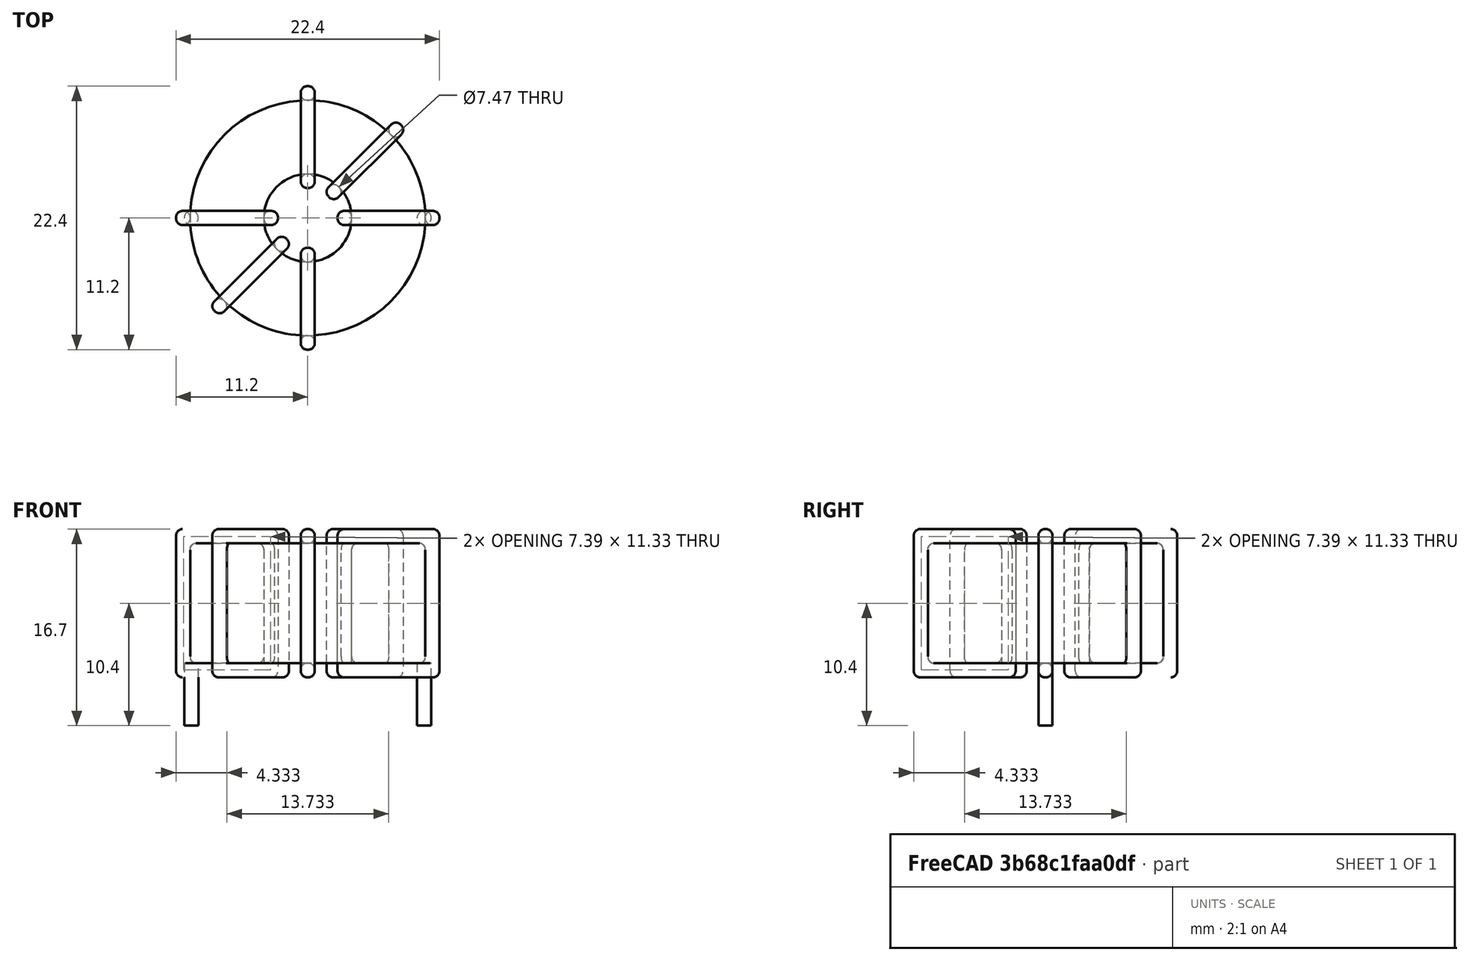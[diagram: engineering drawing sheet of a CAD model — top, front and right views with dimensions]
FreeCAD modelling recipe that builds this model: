
FCSTD DOCUMENT  (FreeCAD 0.16R6703 (Git))
Label: L_Toroid_Horizontal_D22.4mm_P19.80mm_Vishay_TJ4
License: All rights reserved
LicenseURL: http://en.wikipedia.org/wiki/All_rights_reserved
objects: Sketcher::SketchObject×6, PartDesign::Pad×6, PartDesign::Fillet×5, Spreadsheet::Sheet×1
note: 23 computed .brp shape members not serialized (recipe doc carries the construction recipe); baked Part::Feature solids carry a one-line shape summary decoded from their .brp

FEATURE [Spreadsheet::Sheet] Spreadsheet  label="dimensions"
  cells = A1=Wx; B1(Wx)=22.4; C1(WW)=7.466666666666666; D1=22.4; A2=Wy; B2(Wy)=22.4; D2=22.4; A3=RM; B3(RMx)=19.8; C3(RMy)=0; A4=d_wire; B4(d_wire)=1.2; A5=H; B5(H)=10.2; A6=offsetx; B6(offsetx)=1.299999999999999
FEATURE [Sketcher::SketchObject] Sketch
  Placement = pos=(0,0,1.7) rot=(0,0,1;0rad)
  expr: Placement.Base.z = 0.5 + Spreadsheet.d_wire
  expr: Constraints[0] = Spreadsheet.Wx / 2 - Spreadsheet.d_wire
  expr: Constraints[4] = Spreadsheet.WW / 2
  expr: Constraints[2] = Spreadsheet.RMy / 2
  expr: Constraints[1] = Spreadsheet.RMx / 2
  sketch-geometry (2):
    g0: Circle CenterX=9.9 CenterY=0 CenterZ=0 NormalX=0 NormalY=0 NormalZ=1 Radius=10
    g1: Circle CenterX=9.9 CenterY=0 CenterZ=0 NormalX=0 NormalY=0 NormalZ=1 Radius=3.73333
  constraints (5):
    c: Radius(g0) = 10
    c: DistanceX(g-1,g0) = 9.9
    c: DistanceY(g-1,g0) = 0
    c: Coincident(g1,g0)
    c: Radius(g1) = 3.73333
FEATURE [PartDesign::Pad] Pad
  Length = 10.2
  Length2 = 100
  Placement = pos=(0,0,1.7) rot=(0,0,1;0rad)
  Sketch = -> Sketch
  Type = 0
  expr: Length = Spreadsheet.H
FEATURE [Sketcher::SketchObject] Sketch001
  Placement = pos=(0,0,1.1) rot=(0,0,1;0rad)
  expr: Placement.Base.z = 0.5 + Spreadsheet.d_wire * 0.5
  expr: Constraints[4] = Spreadsheet.RMx
  expr: Constraints[2] = Spreadsheet.RMy
  expr: Constraints[1] = Spreadsheet.d_wire / 2
  sketch-geometry (2):
    g0: Circle CenterX=0 CenterY=0 CenterZ=0 NormalX=0 NormalY=0 NormalZ=1 Radius=0.6
    g1: Circle CenterX=19.8 CenterY=0 CenterZ=0 NormalX=0 NormalY=0 NormalZ=1 Radius=0.6
  constraints (5):
    c: Equal(g0,g1)
    c: Radius(g0) = 0.6
    c: DistanceY(g-1,g1) = 0
    c: Coincident(g0,g-1)
    c: DistanceX(g-1,g1) = 19.8
FEATURE [PartDesign::Pad] Pad001
  Length = 0.6
  Length2 = 4.7
  Placement = pos=(0,0,1.1) rot=(0,0,1;0rad)
  Reversed = true
  Sketch = -> Sketch001
  Type = 4
  expr: Length2 = 3.5 + Spreadsheet.d_wire
  expr: Length = Spreadsheet.d_wire / 2
FEATURE [PartDesign::Fillet] Fillet
  Base = -> Pad [Edge6,Edge3,Edge2]
  Placement = pos=(0,0,1.7) rot=(0,0,1;0rad)
  Radius = 0.5
FEATURE [Sketcher::SketchObject] Sketch003
  Placement = pos=(9.9,0,0) rot=(1,0,0;1.5708rad)
  expr: Placement.Base.x = Spreadsheet.RMx / 2
  expr: Constraints[49] = Spreadsheet.Wx - Spreadsheet.d_wire * 2
  expr: Constraints[44] = Spreadsheet.d_wire
  expr: Constraints[23] = Spreadsheet.H
  expr: Constraints[22] = Spreadsheet.Wx / 2 - Spreadsheet.d_wire
  expr: Placement.Base.y = Spreadsheet.RMy / 2
  expr: Constraints[21] = (Spreadsheet.Wx - Spreadsheet.WW) / 2 - Spreadsheet.d_wire
  expr: Constraints[19] = Spreadsheet.d_wire
  expr: Constraints[17] = Spreadsheet.d_wire
  expr: Constraints[18] = Spreadsheet.d_wire
  expr: Constraints[16] = Spreadsheet.d_wire
  sketch-geometry (16):
    g0: LineSegment StartX=-2.53333 StartY=0.5 StartZ=0 EndX=-11.2 EndY=0.5 EndZ=0
    g1: LineSegment StartX=-11.2 StartY=0.5 StartZ=0 EndX=-11.2 EndY=13.1 EndZ=0
    g2: LineSegment StartX=-11.2 StartY=13.1 StartZ=0 EndX=-2.53333 EndY=13.1 EndZ=0
    g3: LineSegment StartX=-2.53333 StartY=13.1 StartZ=0 EndX=-2.53333 EndY=0.5 EndZ=0
    g4: LineSegment StartX=-10 StartY=11.9 StartZ=0 EndX=-3.73333 EndY=11.9 EndZ=0
    g5: LineSegment StartX=-3.73333 StartY=11.9 StartZ=0 EndX=-3.73333 EndY=1.7 EndZ=0
    g6: LineSegment StartX=-3.73333 StartY=1.7 StartZ=0 EndX=-10 EndY=1.7 EndZ=0
    g7: LineSegment StartX=-10 StartY=1.7 StartZ=0 EndX=-10 EndY=11.9 EndZ=0
    g8: LineSegment StartX=2.53333 StartY=13.1 StartZ=0 EndX=11.2 EndY=13.1 EndZ=0
    g9: LineSegment StartX=11.2 StartY=13.1 StartZ=0 EndX=11.2 EndY=0.5 EndZ=0
    g10: LineSegment StartX=11.2 StartY=0.5 StartZ=0 EndX=2.53333 EndY=0.5 EndZ=0
    g11: LineSegment StartX=2.53333 StartY=0.5 StartZ=0 EndX=2.53333 EndY=13.1 EndZ=0
    g12: LineSegment StartX=3.73333 StartY=11.9 StartZ=0 EndX=10 EndY=11.9 EndZ=0
    g13: LineSegment StartX=10 StartY=11.9 StartZ=0 EndX=10 EndY=1.7 EndZ=0
    g14: LineSegment StartX=10 StartY=1.7 StartZ=0 EndX=3.73333 EndY=1.7 EndZ=0
    g15: LineSegment StartX=3.73333 StartY=1.7 StartZ=0 EndX=3.73333 EndY=11.9 EndZ=0
  constraints (50):
    c: Horizontal(g0)
    c: Coincident(g1,g0)
    c: Vertical(g1)
    c: Coincident(g2,g1)
    c: Horizontal(g2)
    c: Coincident(g3,g2)
    c: Coincident(g3,g0)
    c: Vertical(g3)
    c: Coincident(g4,g5)
    c: Coincident(g5,g6)
    c: Coincident(g6,g7)
    c: Coincident(g7,g4)
    c: Horizontal(g4)
    c: Horizontal(g6)
    c: Vertical(g5)
    c: Vertical(g7)
    c: DistanceX(g1,g4) = 1.2
    c: DistanceY(g4,g1) = 1.2
    c: DistanceX(g5,g0) = 1.2
    c: DistanceY(g0,g5) = 1.2
    c: DistanceY(g-1,g0) = 0.5
    c: DistanceX(g6,g6) = 6.26667
    c: DistanceX(g6,g-1) = 10
    c: DistanceY(g7,g7) = 10.2
    c: Coincident(g8,g9)
    c: Coincident(g9,g10)
    c: Coincident(g10,g11)
    c: Coincident(g11,g8)
    c: Horizontal(g8)
    c: Horizontal(g10)
    c: Vertical(g9)
    c: Vertical(g11)
    c: Coincident(g12,g13)
    c: Coincident(g13,g14)
    c: Coincident(g14,g15)
    c: Coincident(g15,g12)
    c: Horizontal(g12)
    c: Horizontal(g14)
    c: Vertical(g13)
    c: Vertical(g15)
    c: DistanceY(g8,g2) = 0
    c: DistanceY(g10,g0) = 0
    c: DistanceY(g14,g5) = 0
    c: DistanceY(g12,g4) = 0
    c: DistanceX(g8,g12) = 1.2
    c: Equal(g8,g2)
    c: Equal(g12,g4)
    c: Equal(g9,g1)
    c: Equal(g13,g7)
    c: DistanceX(g4,g12) = 20
FEATURE [PartDesign::Pad] Pad002
  Length = 1.2
  Length2 = 100
  Midplane = true
  Placement = pos=(9.9,0,0) rot=(1,0,0;1.5708rad)
  Sketch = -> Sketch003
  Type = 0
  expr: Length = Spreadsheet.d_wire
FEATURE [PartDesign::Fillet] Fillet001
  Base = -> Pad002 [Edge38,Edge41,Edge42,Edge43,Edge29,Edge32,Edge33,Edge34,Edge25,Edge35,Edge36,Edge13,Edge14,Edge15,Edge16,Edge17,Edge18,Edge19,Edge1,Edge2,Edge3,Edge4,Edge5,Edge6,Edge7,Edge37,Edge39,Edge40,Edge20,Edge23,Edge24,Edge21,Edge22,Edge8,Edge9,Edge10,Edge11,Edge12,Edge26,Edge27,+8 more]
  Placement = pos=(9.9,0,0) rot=(1,0,0;1.5708rad)
  Radius = 0.564
  expr: Radius = Spreadsheet.d_wire * 0.47
FEATURE [Sketcher::SketchObject] Sketch004
  Placement = pos=(9.9,0,0) rot=(0.862856,0.357407,0.357407;1.71777rad)
  expr: Placement.Base.x = Spreadsheet.RMx / 2
  expr: Constraints[49] = Spreadsheet.Wx - 2 * Spreadsheet.d_wire
  expr: Constraints[44] = Spreadsheet.d_wire
  expr: Constraints[23] = Spreadsheet.H
  expr: Constraints[22] = Spreadsheet.Wx / 2 - Spreadsheet.d_wire
  expr: Placement.Base.y = Spreadsheet.RMy / 2
  expr: Constraints[21] = (Spreadsheet.Wx - Spreadsheet.WW) / 2 - Spreadsheet.d_wire
  expr: Constraints[19] = Spreadsheet.d_wire
  expr: Constraints[17] = Spreadsheet.d_wire
  expr: Constraints[18] = Spreadsheet.d_wire
  expr: Constraints[16] = Spreadsheet.d_wire
  sketch-geometry (16):
    g0: LineSegment StartX=-2.53333 StartY=0.5 StartZ=0 EndX=-11.2 EndY=0.5 EndZ=0
    g1: LineSegment StartX=-11.2 StartY=0.5 StartZ=0 EndX=-11.2 EndY=13.1 EndZ=0
    g2: LineSegment StartX=-11.2 StartY=13.1 StartZ=0 EndX=-2.53333 EndY=13.1 EndZ=0
    g3: LineSegment StartX=-2.53333 StartY=13.1 StartZ=0 EndX=-2.53333 EndY=0.5 EndZ=0
    g4: LineSegment StartX=-10 StartY=11.9 StartZ=0 EndX=-3.73333 EndY=11.9 EndZ=0
    g5: LineSegment StartX=-3.73333 StartY=11.9 StartZ=0 EndX=-3.73333 EndY=1.7 EndZ=0
    g6: LineSegment StartX=-3.73333 StartY=1.7 StartZ=0 EndX=-10 EndY=1.7 EndZ=0
    g7: LineSegment StartX=-10 StartY=1.7 StartZ=0 EndX=-10 EndY=11.9 EndZ=0
    g8: LineSegment StartX=2.53333 StartY=13.1 StartZ=0 EndX=11.2 EndY=13.1 EndZ=0
    g9: LineSegment StartX=11.2 StartY=13.1 StartZ=0 EndX=11.2 EndY=0.5 EndZ=0
    g10: LineSegment StartX=11.2 StartY=0.5 StartZ=0 EndX=2.53333 EndY=0.5 EndZ=0
    g11: LineSegment StartX=2.53333 StartY=0.5 StartZ=0 EndX=2.53333 EndY=13.1 EndZ=0
    g12: LineSegment StartX=3.73333 StartY=11.9 StartZ=0 EndX=10 EndY=11.9 EndZ=0
    g13: LineSegment StartX=10 StartY=11.9 StartZ=0 EndX=10 EndY=1.7 EndZ=0
    g14: LineSegment StartX=10 StartY=1.7 StartZ=0 EndX=3.73333 EndY=1.7 EndZ=0
    g15: LineSegment StartX=3.73333 StartY=1.7 StartZ=0 EndX=3.73333 EndY=11.9 EndZ=0
  constraints (50):
    c: Horizontal(g0)
    c: Coincident(g1,g0)
    c: Vertical(g1)
    c: Coincident(g2,g1)
    c: Horizontal(g2)
    c: Coincident(g3,g2)
    c: Coincident(g3,g0)
    c: Vertical(g3)
    c: Coincident(g4,g5)
    c: Coincident(g5,g6)
    c: Coincident(g6,g7)
    c: Coincident(g7,g4)
    c: Horizontal(g4)
    c: Horizontal(g6)
    c: Vertical(g5)
    c: Vertical(g7)
    c: DistanceX(g1,g4) = 1.2
    c: DistanceY(g4,g1) = 1.2
    c: DistanceX(g5,g0) = 1.2
    c: DistanceY(g0,g5) = 1.2
    c: DistanceY(g-1,g0) = 0.5
    c: DistanceX(g6,g6) = 6.26667
    c: DistanceX(g6,g-1) = 10
    c: DistanceY(g7,g7) = 10.2
    c: Coincident(g8,g9)
    c: Coincident(g9,g10)
    c: Coincident(g10,g11)
    c: Coincident(g11,g8)
    c: Horizontal(g8)
    c: Horizontal(g10)
    c: Vertical(g9)
    c: Vertical(g11)
    c: Coincident(g12,g13)
    c: Coincident(g13,g14)
    c: Coincident(g14,g15)
    c: Coincident(g15,g12)
    c: Horizontal(g12)
    c: Horizontal(g14)
    c: Vertical(g13)
    c: Vertical(g15)
    c: DistanceY(g8,g2) = 0
    c: DistanceY(g10,g0) = 0
    c: DistanceY(g14,g5) = 0
    c: DistanceY(g12,g4) = 0
    c: DistanceX(g8,g12) = 1.2
    c: Equal(g8,g2)
    c: Equal(g12,g4)
    c: Equal(g9,g1)
    c: Equal(g13,g7)
    c: DistanceX(g4,g12) = 20
FEATURE [PartDesign::Pad] Pad003
  Length = 1.2
  Length2 = 100
  Midplane = true
  Placement = pos=(9.9,0,0) rot=(0.862856,0.357407,0.357407;1.71777rad)
  Sketch = -> Sketch004
  Type = 0
  expr: Length = Spreadsheet.d_wire
FEATURE [PartDesign::Fillet] Fillet002
  Base = -> Pad003 [Edge38,Edge41,Edge42,Edge43,Edge29,Edge32,Edge33,Edge34,Edge25,Edge35,Edge36,Edge13,Edge14,Edge15,Edge16,Edge17,Edge18,Edge19,Edge1,Edge2,Edge3,Edge4,Edge5,Edge6,Edge7,Edge37,Edge39,Edge40,Edge20,Edge23,Edge24,Edge21,Edge22,Edge8,Edge9,Edge10,Edge11,Edge12,Edge26,Edge27,+8 more]
  Placement = pos=(9.9,0,0) rot=(0.862856,0.357407,0.357407;1.71777rad)
  Radius = 0.564
  expr: Radius = Spreadsheet.d_wire * 0.47
FEATURE [Sketcher::SketchObject] Sketch005
  Placement = pos=(9.9,0,0) rot=(0.862856,-0.357407,-0.357407;1.71777rad)
  expr: Placement.Base.x = Spreadsheet.RMx / 2
  expr: Constraints[49] = Spreadsheet.Wx - 2 * Spreadsheet.d_wire
  expr: Constraints[44] = Spreadsheet.d_wire
  expr: Constraints[23] = Spreadsheet.H
  expr: Constraints[22] = Spreadsheet.Wx / 2 - Spreadsheet.d_wire
  expr: Placement.Base.y = Spreadsheet.RMy / 2
  expr: Constraints[21] = (Spreadsheet.Wx - Spreadsheet.WW) / 2 - Spreadsheet.d_wire
  expr: Constraints[19] = Spreadsheet.d_wire
  expr: Constraints[17] = Spreadsheet.d_wire
  expr: Constraints[18] = Spreadsheet.d_wire
  expr: Constraints[16] = Spreadsheet.d_wire
  sketch-geometry (16):
    g0: LineSegment StartX=-2.53333 StartY=0.5 StartZ=0 EndX=-11.2 EndY=0.5 EndZ=0
    g1: LineSegment StartX=-11.2 StartY=0.5 StartZ=0 EndX=-11.2 EndY=13.1 EndZ=0
    g2: LineSegment StartX=-11.2 StartY=13.1 StartZ=0 EndX=-2.53333 EndY=13.1 EndZ=0
    g3: LineSegment StartX=-2.53333 StartY=13.1 StartZ=0 EndX=-2.53333 EndY=0.5 EndZ=0
    g4: LineSegment StartX=-10 StartY=11.9 StartZ=0 EndX=-3.73333 EndY=11.9 EndZ=0
    g5: LineSegment StartX=-3.73333 StartY=11.9 StartZ=0 EndX=-3.73333 EndY=1.7 EndZ=0
    g6: LineSegment StartX=-3.73333 StartY=1.7 StartZ=0 EndX=-10 EndY=1.7 EndZ=0
    g7: LineSegment StartX=-10 StartY=1.7 StartZ=0 EndX=-10 EndY=11.9 EndZ=0
    g8: LineSegment StartX=2.53333 StartY=13.1 StartZ=0 EndX=11.2 EndY=13.1 EndZ=0
    g9: LineSegment StartX=11.2 StartY=13.1 StartZ=0 EndX=11.2 EndY=0.5 EndZ=0
    g10: LineSegment StartX=11.2 StartY=0.5 StartZ=0 EndX=2.53333 EndY=0.5 EndZ=0
    g11: LineSegment StartX=2.53333 StartY=0.5 StartZ=0 EndX=2.53333 EndY=13.1 EndZ=0
    g12: LineSegment StartX=3.73333 StartY=11.9 StartZ=0 EndX=10 EndY=11.9 EndZ=0
    g13: LineSegment StartX=10 StartY=11.9 StartZ=0 EndX=10 EndY=1.7 EndZ=0
    g14: LineSegment StartX=10 StartY=1.7 StartZ=0 EndX=3.73333 EndY=1.7 EndZ=0
    g15: LineSegment StartX=3.73333 StartY=1.7 StartZ=0 EndX=3.73333 EndY=11.9 EndZ=0
  constraints (50):
    c: Horizontal(g0)
    c: Coincident(g1,g0)
    c: Vertical(g1)
    c: Coincident(g2,g1)
    c: Horizontal(g2)
    c: Coincident(g3,g2)
    c: Coincident(g3,g0)
    c: Vertical(g3)
    c: Coincident(g4,g5)
    c: Coincident(g5,g6)
    c: Coincident(g6,g7)
    c: Coincident(g7,g4)
    c: Horizontal(g4)
    c: Horizontal(g6)
    c: Vertical(g5)
    c: Vertical(g7)
    c: DistanceX(g1,g4) = 1.2
    c: DistanceY(g4,g1) = 1.2
    c: DistanceX(g5,g0) = 1.2
    c: DistanceY(g0,g5) = 1.2
    c: DistanceY(g-1,g0) = 0.5
    c: DistanceX(g6,g6) = 6.26667
    c: DistanceX(g6,g-1) = 10
    c: DistanceY(g7,g7) = 10.2
    c: Coincident(g8,g9)
    c: Coincident(g9,g10)
    c: Coincident(g10,g11)
    c: Coincident(g11,g8)
    c: Horizontal(g8)
    c: Horizontal(g10)
    c: Vertical(g9)
    c: Vertical(g11)
    c: Coincident(g12,g13)
    c: Coincident(g13,g14)
    c: Coincident(g14,g15)
    c: Coincident(g15,g12)
    c: Horizontal(g12)
    c: Horizontal(g14)
    c: Vertical(g13)
    c: Vertical(g15)
    c: DistanceY(g8,g2) = 0
    c: DistanceY(g10,g0) = 0
    c: DistanceY(g14,g5) = 0
    c: DistanceY(g12,g4) = 0
    c: DistanceX(g8,g12) = 1.2
    c: Equal(g8,g2)
    c: Equal(g12,g4)
    c: Equal(g9,g1)
    c: Equal(g13,g7)
    c: DistanceX(g4,g12) = 20
FEATURE [PartDesign::Pad] Pad004
  Length = 1.2
  Length2 = 100
  Midplane = true
  Placement = pos=(9.9,0,0) rot=(0.862856,-0.357407,-0.357407;1.71777rad)
  Sketch = -> Sketch005
  Type = 0
  expr: Length = Spreadsheet.d_wire
FEATURE [PartDesign::Fillet] Fillet003
  Base = -> Pad004 [Edge38,Edge41,Edge42,Edge43,Edge29,Edge32,Edge33,Edge34,Edge25,Edge35,Edge36,Edge13,Edge14,Edge15,Edge16,Edge17,Edge18,Edge19,Edge1,Edge2,Edge3,Edge4,Edge5,Edge6,Edge7,Edge37,Edge39,Edge40,Edge20,Edge23,Edge24,Edge21,Edge22,Edge8,Edge9,Edge10,Edge11,Edge12,Edge26,Edge27,+8 more]
  Placement = pos=(9.9,0,0) rot=(0.862856,-0.357407,-0.357407;1.71777rad)
  Radius = 0.564
  expr: Radius = Spreadsheet.d_wire * 0.47
FEATURE [Sketcher::SketchObject] Sketch006
  Placement = pos=(9.9,0,0) rot=(0.57735,0.57735,0.57735;2.0944rad)
  expr: Placement.Base.x = Spreadsheet.RMx / 2
  expr: Constraints[49] = Spreadsheet.Wx - Spreadsheet.d_wire * 2
  expr: Constraints[44] = Spreadsheet.d_wire
  expr: Constraints[23] = Spreadsheet.H
  expr: Constraints[22] = Spreadsheet.Wx / 2 - Spreadsheet.d_wire
  expr: Placement.Base.y = Spreadsheet.RMy / 2
  expr: Constraints[21] = (Spreadsheet.Wx - Spreadsheet.WW) / 2 - Spreadsheet.d_wire
  expr: Constraints[19] = Spreadsheet.d_wire
  expr: Constraints[17] = Spreadsheet.d_wire
  expr: Constraints[18] = Spreadsheet.d_wire
  expr: Constraints[16] = Spreadsheet.d_wire
  sketch-geometry (16):
    g0: LineSegment StartX=-2.53333 StartY=0.5 StartZ=0 EndX=-11.2 EndY=0.5 EndZ=0
    g1: LineSegment StartX=-11.2 StartY=0.5 StartZ=0 EndX=-11.2 EndY=13.1 EndZ=0
    g2: LineSegment StartX=-11.2 StartY=13.1 StartZ=0 EndX=-2.53333 EndY=13.1 EndZ=0
    g3: LineSegment StartX=-2.53333 StartY=13.1 StartZ=0 EndX=-2.53333 EndY=0.5 EndZ=0
    g4: LineSegment StartX=-10 StartY=11.9 StartZ=0 EndX=-3.73333 EndY=11.9 EndZ=0
    g5: LineSegment StartX=-3.73333 StartY=11.9 StartZ=0 EndX=-3.73333 EndY=1.7 EndZ=0
    g6: LineSegment StartX=-3.73333 StartY=1.7 StartZ=0 EndX=-10 EndY=1.7 EndZ=0
    g7: LineSegment StartX=-10 StartY=1.7 StartZ=0 EndX=-10 EndY=11.9 EndZ=0
    g8: LineSegment StartX=2.53333 StartY=13.1 StartZ=0 EndX=11.2 EndY=13.1 EndZ=0
    g9: LineSegment StartX=11.2 StartY=13.1 StartZ=0 EndX=11.2 EndY=0.5 EndZ=0
    g10: LineSegment StartX=11.2 StartY=0.5 StartZ=0 EndX=2.53333 EndY=0.5 EndZ=0
    g11: LineSegment StartX=2.53333 StartY=0.5 StartZ=0 EndX=2.53333 EndY=13.1 EndZ=0
    g12: LineSegment StartX=3.73333 StartY=11.9 StartZ=0 EndX=10 EndY=11.9 EndZ=0
    g13: LineSegment StartX=10 StartY=11.9 StartZ=0 EndX=10 EndY=1.7 EndZ=0
    g14: LineSegment StartX=10 StartY=1.7 StartZ=0 EndX=3.73333 EndY=1.7 EndZ=0
    g15: LineSegment StartX=3.73333 StartY=1.7 StartZ=0 EndX=3.73333 EndY=11.9 EndZ=0
  constraints (50):
    c: Horizontal(g0)
    c: Coincident(g1,g0)
    c: Vertical(g1)
    c: Coincident(g2,g1)
    c: Horizontal(g2)
    c: Coincident(g3,g2)
    c: Coincident(g3,g0)
    c: Vertical(g3)
    c: Coincident(g4,g5)
    c: Coincident(g5,g6)
    c: Coincident(g6,g7)
    c: Coincident(g7,g4)
    c: Horizontal(g4)
    c: Horizontal(g6)
    c: Vertical(g5)
    c: Vertical(g7)
    c: DistanceX(g1,g4) = 1.2
    c: DistanceY(g4,g1) = 1.2
    c: DistanceX(g5,g0) = 1.2
    c: DistanceY(g0,g5) = 1.2
    c: DistanceY(g-1,g0) = 0.5
    c: DistanceX(g6,g6) = 6.26667
    c: DistanceX(g6,g-1) = 10
    c: DistanceY(g7,g7) = 10.2
    c: Coincident(g8,g9)
    c: Coincident(g9,g10)
    c: Coincident(g10,g11)
    c: Coincident(g11,g8)
    c: Horizontal(g8)
    c: Horizontal(g10)
    c: Vertical(g9)
    c: Vertical(g11)
    c: Coincident(g12,g13)
    c: Coincident(g13,g14)
    c: Coincident(g14,g15)
    c: Coincident(g15,g12)
    c: Horizontal(g12)
    c: Horizontal(g14)
    c: Vertical(g13)
    c: Vertical(g15)
    c: DistanceY(g8,g2) = 0
    c: DistanceY(g10,g0) = 0
    c: DistanceY(g14,g5) = 0
    c: DistanceY(g12,g4) = 0
    c: DistanceX(g8,g12) = 1.2
    c: Equal(g8,g2)
    c: Equal(g12,g4)
    c: Equal(g9,g1)
    c: Equal(g13,g7)
    c: DistanceX(g4,g12) = 20
FEATURE [PartDesign::Pad] Pad005
  Length = 1.2
  Length2 = 100
  Midplane = true
  Placement = pos=(9.9,0,0) rot=(0.57735,0.57735,0.57735;2.0944rad)
  Sketch = -> Sketch006
  Type = 0
  expr: Length = Spreadsheet.d_wire
FEATURE [PartDesign::Fillet] Fillet004
  Base = -> Pad005 [Edge38,Edge41,Edge42,Edge43,Edge29,Edge32,Edge33,Edge34,Edge25,Edge35,Edge36,Edge13,Edge14,Edge15,Edge16,Edge17,Edge18,Edge19,Edge1,Edge2,Edge3,Edge4,Edge5,Edge6,Edge7,Edge37,Edge39,Edge40,Edge20,Edge23,Edge24,Edge21,Edge22,Edge8,Edge9,Edge10,Edge11,Edge12,Edge26,Edge27,+8 more]
  Placement = pos=(9.9,0,0) rot=(0.57735,0.57735,0.57735;2.0944rad)
  Radius = 0.564
  expr: Radius = Spreadsheet.d_wire * 0.47
